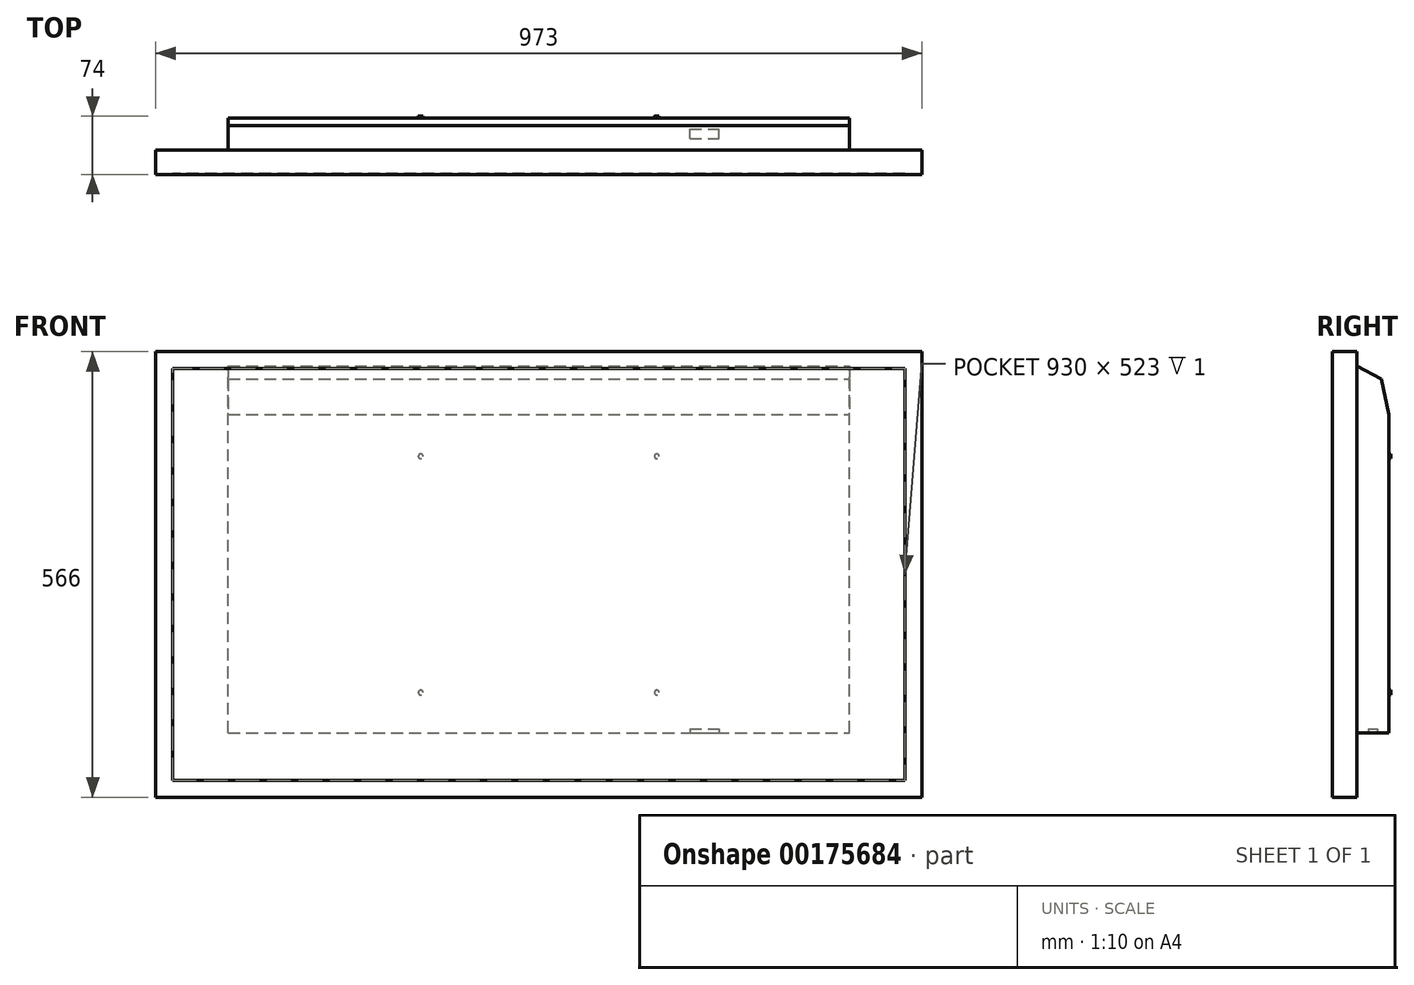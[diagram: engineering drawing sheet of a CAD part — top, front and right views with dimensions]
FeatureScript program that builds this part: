
annotation { "Feature Type Name" : "Feature", "Feature Type Description" : "" }
export const myFeature = defineFeature(function(context is Context, id is Id, definition is map)
    precondition{}
    {
        {
            var Q0;
            Q0=qCreatedBy(makeId("Front.planeOp"),FACE);
            var sketch = newSketch(context, id + "F0", { "sketchPlane" : qUnion([Q0])});
            skLineSegment(sketch, "E0.bottom", {"start": v(486.5, -283) * mm, "end": v(-486.5, -283) * mm});
            skLineSegment(sketch, "E0.top", {"start": v(486.5, 283) * mm, "end": v(-486.5, 283) * mm});
            skLineSegment(sketch, "E0.left", {"start": v(486.5, -283) * mm, "end": v(486.5, 283) * mm});
            skLineSegment(sketch, "E0.right", {"start": v(-486.5, -283) * mm, "end": v(-486.5, 283) * mm});
            skPoint(sketch, "E0.middle", {"position": v(0, 0) * mm});
            skSolve(sketch);
        }
        {
            var Q0;
            Q0=qSketchRegion(id+"F0",true);
            extrude(context, id + "F1", {"entities" : qUnion([Q0]), "depth" : 31 * mm});
        }
        {
            var Q0;
            Q0=makeQuery(id+"F1.opExtrude","CAP_FACE",FACE,{"disambiguationData":[OSD([sQuery(id+"F0.wireOp",EDGE,"E0.bottom"),sQuery(id+"F0.wireOp",EDGE,"E0.top"),sQuery(id+"F0.wireOp",EDGE,"E0.left"),sQuery(id+"F0.wireOp",EDGE,"E0.right")])],"isStart":true});
            var sketch = newSketch(context, id + "F2", { "sketchPlane" : qUnion([Q0])});
            skPoint(sketch, "E1.middle", {"position": v(0, 0) * mm});
            skLineSegment(sketch, "E2", {"start": v(0, 283) * mm, "end": v(0, -283) * mm, "construction": true});
            skLineSegment(sketch, "E3.bottom", {"start": v(394.5, -201) * mm, "end": v(-394.5, -201) * mm});
            skLineSegment(sketch, "E3.top", {"start": v(394.5, 265) * mm, "end": v(-394.5, 265) * mm});
            skLineSegment(sketch, "E3.left", {"start": v(394.5, -201) * mm, "end": v(394.5, 265) * mm});
            skLineSegment(sketch, "E3.right", {"start": v(-394.5, -201) * mm, "end": v(-394.5, 265) * mm});
            skPoint(sketch, "E3.middle", {"position": v(0, 32) * mm});
            skSolve(sketch);
        }
        {
            var Q0;
            Q0=qSketchRegion(id+"F2",true);
            extrude(context, id + "F3", {"entities" : qUnion([Q0]), "operationType" : NewBodyOperationType.ADD, "depth" : 41 * mm});
        }
        {
            var Q0;
            Q0=makeQuery(id+"F3.opExtrude","SWEPT_FACE",FACE,{"disambiguationData":[OSD([sQuery(id+"F2.wireOp",EDGE,"E3.bottom")])]});
            var sketch = newSketch(context, id + "F4", { "sketchPlane" : qUnion([Q0])});
            skLineSegment(sketch, "E4", {"start": v(394.5, -20.5) * mm, "end": v(-394.5, -20.5) * mm, "construction": true});
            skLineSegment(sketch, "E5.bottom", {"start": v(191.87, -14.53) * mm, "end": v(228.87, -14.53) * mm});
            skLineSegment(sketch, "E5.top", {"start": v(191.87, -26.47) * mm, "end": v(228.87, -26.47) * mm});
            skLineSegment(sketch, "E5.left", {"start": v(191.87, -14.53) * mm, "end": v(191.87, -26.47) * mm});
            skLineSegment(sketch, "E5.right", {"start": v(228.87, -14.53) * mm, "end": v(228.87, -26.47) * mm});
            skPoint(sketch, "E5.middle", {"position": v(210.37, -20.5) * mm});
            skSolve(sketch);
        }
        {
            var Q0;
            Q0=qSketchRegion(id+"F4",true);
            extrude(context, id + "F5", {"entities" : qUnion([Q0]), "operationType" : NewBodyOperationType.REMOVE, "oppositeDirection" : true, "depth" : 5 * mm});
        }
        {
            var Q0;
            Q0=makeQuery(id+"F1.opExtrude","CAP_FACE",FACE,{"disambiguationData":[OSD([sQuery(id+"F0.wireOp",EDGE,"E0.bottom"),sQuery(id+"F0.wireOp",EDGE,"E0.top"),sQuery(id+"F0.wireOp",EDGE,"E0.left"),sQuery(id+"F0.wireOp",EDGE,"E0.right")])],"isStart":false});
            var sketch = newSketch(context, id + "F6", { "sketchPlane" : qUnion([Q0])});
            skLineSegment(sketch, "E6.bottom", {"start": v(465, -261.5) * mm, "end": v(-465, -261.5) * mm});
            skLineSegment(sketch, "E6.top", {"start": v(465, 261.5) * mm, "end": v(-465, 261.5) * mm});
            skLineSegment(sketch, "E6.left", {"start": v(465, -261.5) * mm, "end": v(465, 261.5) * mm});
            skLineSegment(sketch, "E6.right", {"start": v(-465, -261.5) * mm, "end": v(-465, 261.5) * mm});
            skPoint(sketch, "E6.middle", {"position": v(0, 0) * mm});
            skSolve(sketch);
        }
        {
            var Q0;
            Q0=qSketchRegion(id+"F6",true);
            extrude(context, id + "F7", {"entities" : qUnion([Q0]), "operationType" : NewBodyOperationType.REMOVE, "oppositeDirection" : true, "depth" : 1 * mm});
        }
        {
            var Q0;
            Q0=makeQuery(id+"F1.opExtrude","CAP_FACE",FACE,{"disambiguationData":[OSD([sQuery(id+"F0.wireOp",EDGE,"E0.bottom"),sQuery(id+"F0.wireOp",EDGE,"E0.top"),sQuery(id+"F0.wireOp",EDGE,"E0.left"),sQuery(id+"F0.wireOp",EDGE,"E0.right")])],"isStart":true});
            var sketch = newSketch(context, id + "F8", { "sketchPlane" : qUnion([Q0])});
            skLineSegment(sketch, "E7", {"start": v(486.5, 0) * mm, "end": v(-486.5, 0) * mm, "construction": true});
            skLineSegment(sketch, "E8", {"start": v(0, -283) * mm, "end": v(0, 283) * mm, "construction": true});
            skCircle(sketch, "E9", {"center": v(-150, 150) * mm, "radius": 3 * mm});
            skCircle(sketch, "E10.MirrorC", {"center": v(150, 150) * mm, "radius": 3 * mm});
            skCircle(sketch, "E11.MirrorC", {"center": v(-150, -150) * mm, "radius": 3 * mm});
            skCircle(sketch, "E12.MirrorC", {"center": v(150, -150) * mm, "radius": 3 * mm});
            skSolve(sketch);
        }
        {
            var Q0;
            Q0 = qSketchRegion(id + "F8", true);
            extrude(context, id + "F9", {"entities" : qUnion([Q0]), "operationType" : NewBodyOperationType.ADD, "depth" : 43 * mm});
        }
        {
            var Q0;
            Q0=makeQuery(id+"F3.opExtrude","SWEPT_FACE",FACE,{"disambiguationData":[OSD([sQuery(id+"F2.wireOp",EDGE,"E3.right")])]});
            var sketch = newSketch(context, id + "F10", { "sketchPlane" : qUnion([Q0])});
            skLineSegment(sketch, "E13", {"start": v(0, 265) * mm, "end": v(31, 248) * mm});
            skLineSegment(sketch, "E14", {"start": v(31, 248) * mm, "end": v(41, 203) * mm});
            skLineSegment(sketch, "E15", {"start": v(41, 203) * mm, "end": v(41, 265) * mm});
            skLineSegment(sketch, "E16", {"start": v(41, 265) * mm, "end": v(0, 265) * mm});
            skSolve(sketch);
        }
        {
            var Q0;
            Q0 = qSketchRegion(id + "F10", true);
            extrude(context, id + "F11", {"entities" : qUnion([Q0]), "operationType" : NewBodyOperationType.REMOVE, "endBound" : BoundingType.THROUGH_ALL, "oppositeDirection" : true, "depth" : 25 * mm});
        }
    });
